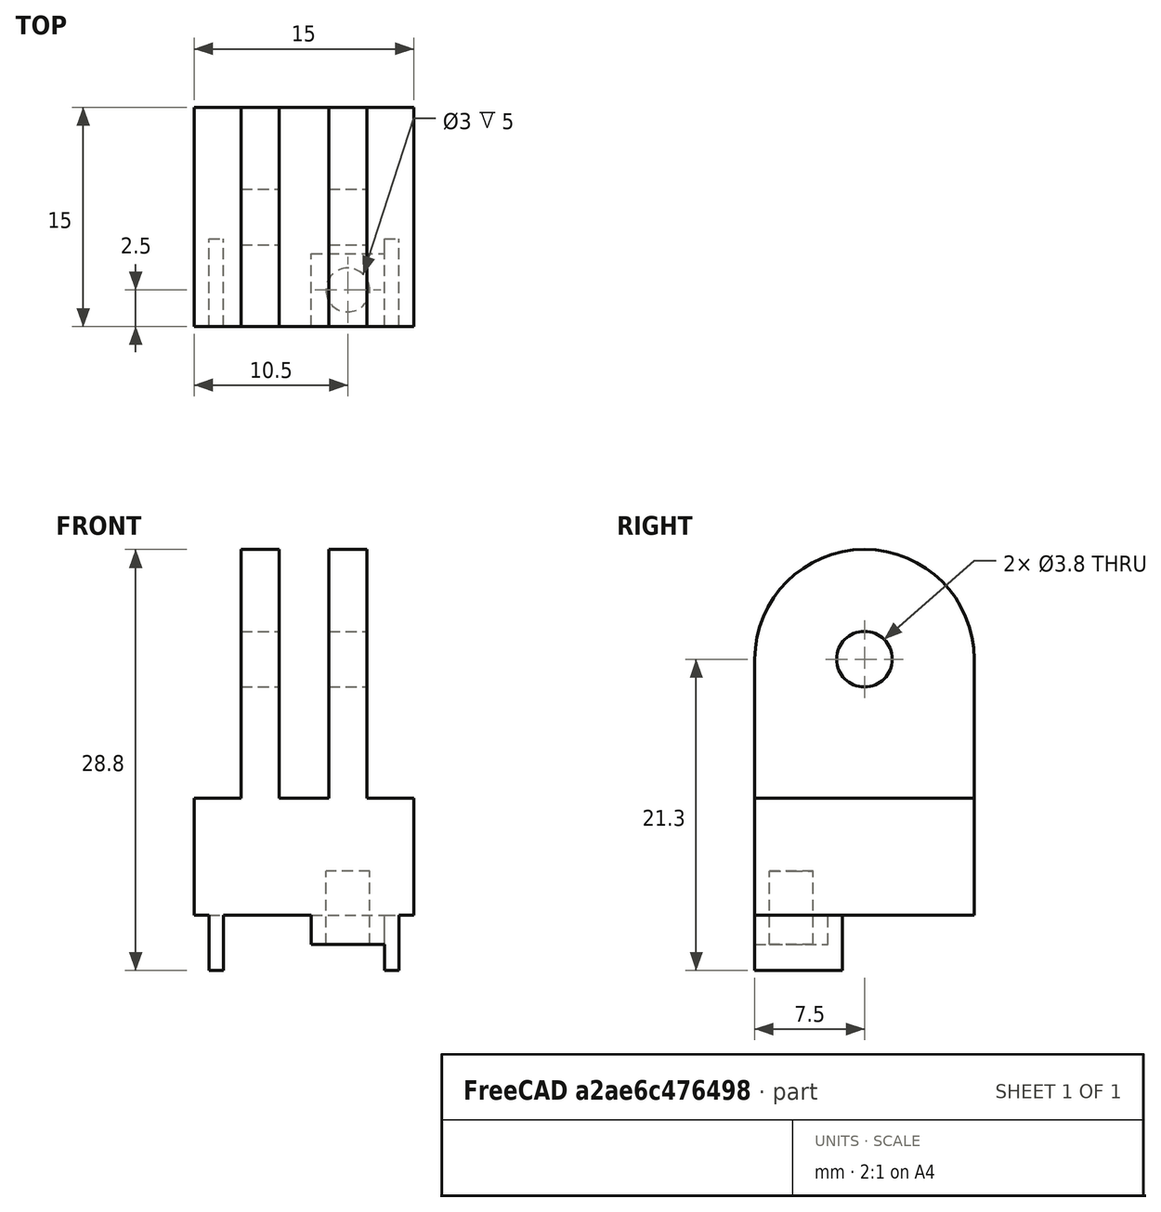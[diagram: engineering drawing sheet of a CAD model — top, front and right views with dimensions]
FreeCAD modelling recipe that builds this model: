
FCSTD DOCUMENT  (FreeCAD 0.18.4R)
Label: gy6180
License: FreeArt
LicenseURL: http://artlibre.org/licence/lal
objects: Part::Box×3, Spreadsheet::Sheet×1, Part::Feature×1, Part::Cylinder×1, Part::FeaturePython×1, Part::MultiFuse×1, Part::Cut×1, App::Part×1
note: 8 computed .brp shape members not serialized (recipe doc carries the construction recipe); baked Part::Feature solids carry a one-line shape summary decoded from their .brp

FEATURE [Spreadsheet::Sheet] Spreadsheet  label="p"
  cells = A1=pcb_x; B1(pcb_x)=11; A2=pcb_y; B2(pcb_y)=14; A3=pcb_z; B3(pcb_z)=1.8; A4=pcb_fwd; B4(pcb_fwd)=2; A5=pcb_back; B5(pcb_back)=2; A6=stand_x; B6(stand_x)=5; A7=stand_y; B7(stand_y)=5; A8=hole_r; B8(hole_r)=1.5; A9=sensor_hole_x; B9(sensor_hole_x)=2.6; A10=sensor_hole_y; B10(sensor_hole_y)=4.5; A11=wall; B11(wall)=3; A12=stick_width; B12(stick_width)=15; A13=stick_length; B13(stick_length)=5; A14=side_wall; B14(side_wall)=1; A15=side_wall_y; B15(side_wall_y)==p.stand_y + p.side_wall
FEATURE [Part::Box] Box  label="stand cube"
  AttacherType = Attacher::AttachEngine3D
  Height = 5
  Length = 5
  Placement = pos=(8,0,0) rot=(0,0,1;0rad)
  Width = 5
  expr: Placement.Base.x = (p.stick_width + p.pcb_x) / 2 - p.stand_x
  expr: Height = p.pcb_back + p.wall
  expr: Width = p.stand_y
  expr: Length = p.stand_x
FEATURE [Part::Feature] Cut001001  label="side 2 cut001"
  Placement = pos=(7.5,7.5,7) rot=(0,0,1;1.5708rad)
  shape: bbox 15 x 15 x 20 mm, 16 faces (baked)
  expr: Placement.Base.z = p.pcb_back + p.stick_length
  expr: Placement.Base.x = p.stick_width / 2
  expr: Placement.Base.y = p.stick_width / 2
FEATURE [Part::Cylinder] Cylinder  label="bolt hole"
  Angle = 360
  AttacherType = Attacher::AttachEngine3D
  Height = 5
  Placement = pos=(10.5,2.5,0) rot=(0,0,1;0rad)
  Radius = 1.5
  expr: Placement.Base.x = (p.stick_width + p.pcb_x) / 2 - p.stand_x / 2
  expr: Placement.Base.y = p.hole_off_y
  expr: Height = p.pcb_back + p.wall
  expr: Radius = p.hole_r
FEATURE [Part::Box] Box002  label="stick cube"
  AttacherType = Attacher::AttachEngine3D
  Height = 5
  Length = 15
  Placement = pos=(0,0,2) rot=(0,0,1;0rad)
  Width = 15
  expr: Height = p.stick_length
  expr: Placement.Base.z = p.pcb_back
  expr: Width = p.stick_width
  expr: Length = p.stick_width
FEATURE [Part::Box] Box004  label="side wall"
  AttacherType = Attacher::AttachEngine3D
  Height = 3.8
  Length = 1
  Placement = pos=(0,1,0) rot=(0,0,1;0rad)
  Width = 6
  expr: Placement.Base.y = p.side_wall
  expr: Height = p.pcb_back + p.pcb_z
  expr: Width = p.side_wall_y
  expr: Length = p.side_wall
FEATURE [Part::FeaturePython] Array  label="side wall array"  # Draft array (typed FeaturePython)
  Angle = 360
  ArrayType = 0
  Axis = (0,0,1)
  Base = -> Box004
  Center = (0,0,0)
  Fuse = false
  IntervalAxis = (0,0,0)
  IntervalX = (12,0,0)
  IntervalY = (0,1,0)
  IntervalZ = (0,0,1)
  NumberPolar = 1
  NumberX = 2
  NumberY = 1
  NumberZ = 1
  Placement = pos=(1,-1,-1.8) rot=(0,0,1;0rad)
  expr: Placement.Base.z = -p.pcb_z
  expr: Placement.Base.y = -p.side_wall
  expr: Placement.Base.x = (p.stick_width - p.pcb_x) / 2 - p.side_wall
  expr: IntervalX.x = p.pcb_x + p.side_wall
FEATURE [Part::MultiFuse] Fusion  label="holder fusion"
  Shapes = -> [Box,Cut001001,Box002,Array]
FEATURE [Part::Cut] Cut  label="gy6180 sensor cut"
  Base = -> Fusion
  Tool = -> Cylinder
FEATURE [App::Part] Part  label="gy6180 sensor part"
  Group = -> [Fusion,Box002,Cylinder,Box,Cut001001,Cut]
  Origin = -> Origin
